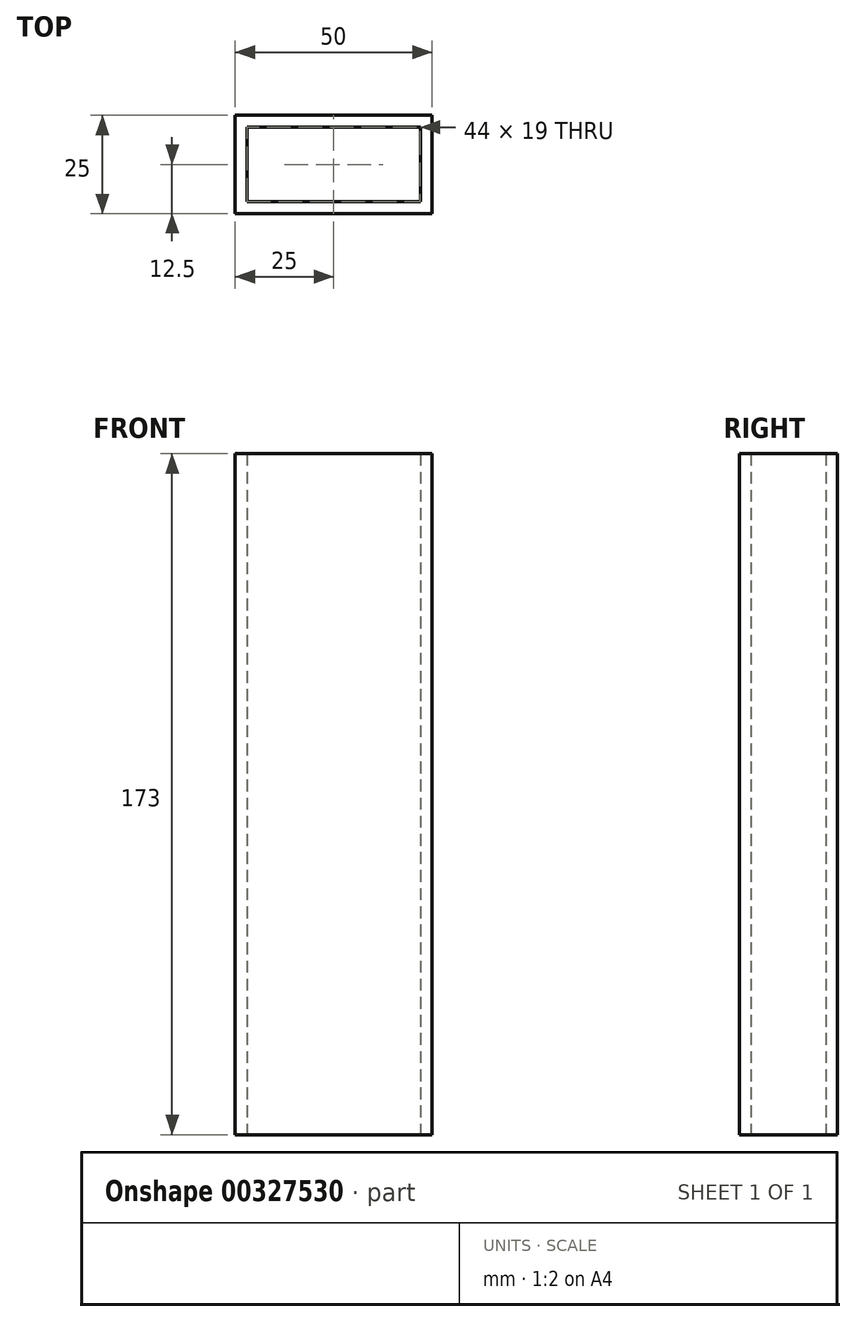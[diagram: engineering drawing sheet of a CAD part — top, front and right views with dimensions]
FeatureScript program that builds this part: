
annotation { "Feature Type Name" : "Feature", "Feature Type Description" : "" }
export const myFeature = defineFeature(function(context is Context, id is Id, definition is map)
    precondition{}
    {
        {
            var Q0;
            Q0=qCreatedBy(makeId("Top.planeOp"),FACE);
            var sketch = newSketch(context, id + "F0", { "sketchPlane" : qUnion([Q0])});
            skLineSegment(sketch, "E0.bottom", {"start": v(-25, -12.5) * mm, "end": v(25, -12.5) * mm});
            skLineSegment(sketch, "E0.top", {"start": v(-25, 12.5) * mm, "end": v(25, 12.5) * mm});
            skLineSegment(sketch, "E0.left", {"start": v(-25, -12.5) * mm, "end": v(-25, 12.5) * mm});
            skLineSegment(sketch, "E0.right", {"start": v(25, -12.5) * mm, "end": v(25, 12.5) * mm});
            skPoint(sketch, "E0.middle", {"position": v(0, 0) * mm});
            skLineSegment(sketch, "E1.bottom", {"start": v(22, -9.5) * mm, "end": v(-22, -9.5) * mm});
            skLineSegment(sketch, "E1.top", {"start": v(22, 9.5) * mm, "end": v(-22, 9.5) * mm});
            skLineSegment(sketch, "E1.left", {"start": v(22, -9.5) * mm, "end": v(22, 9.5) * mm});
            skLineSegment(sketch, "E1.right", {"start": v(-22, -9.5) * mm, "end": v(-22, 9.5) * mm});
            skSolve(sketch);
        }
        {
            var Q0;
            Q0 = qSketchRegion(id + "F0", true);
            extrude(context, id + "F1", {"entities" : qUnion([Q0]), "depth" : 173 * mm, "symmetric" : true});
        }
    });
